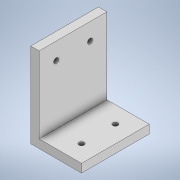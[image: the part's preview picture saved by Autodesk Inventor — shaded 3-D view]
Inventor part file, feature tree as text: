
AUTODESK INVENTOR PART (.ipt)
format: ipt  version: 2021 (Build 250183000, 183)  size: 114,176 bytes
history: native  units: mm
features: sketch x5, extrude x3
ambient origin geometry x8: Origin, YZ Plane, XZ Plane, XY Plane, X Axis, Y Axis, Z Axis, Center Point
bodies: Solid1 (feature_tree)
feature tree (8):
  extrude  "Extrusion1"  Depth=5.0mm
  sketch  "Sketch2"  dims[d2=45.0mm d3=25.0mm]
  sketch  "Sketch3"  dims[d4=5.0mm d5=40.0mm d6=0.0mm]
  extrude  "Extrusion2"  Depth=25.0mm
  sketch  "Sketch4"  dims[d7=3.0mm]
  extrude  "Extrusion3"  Depth=40.0mm TaperAngle=0.0deg
  sketch  "Sketch1"  dims[d0=50.0mm d1=5.0mm]
  sketch  "Sketch5"  dims[d8=3.0mm d9=0.0mm d10=0.0mm d11=3.0mm d12=3.0mm d13=0.0mm d14=0.0mm]
